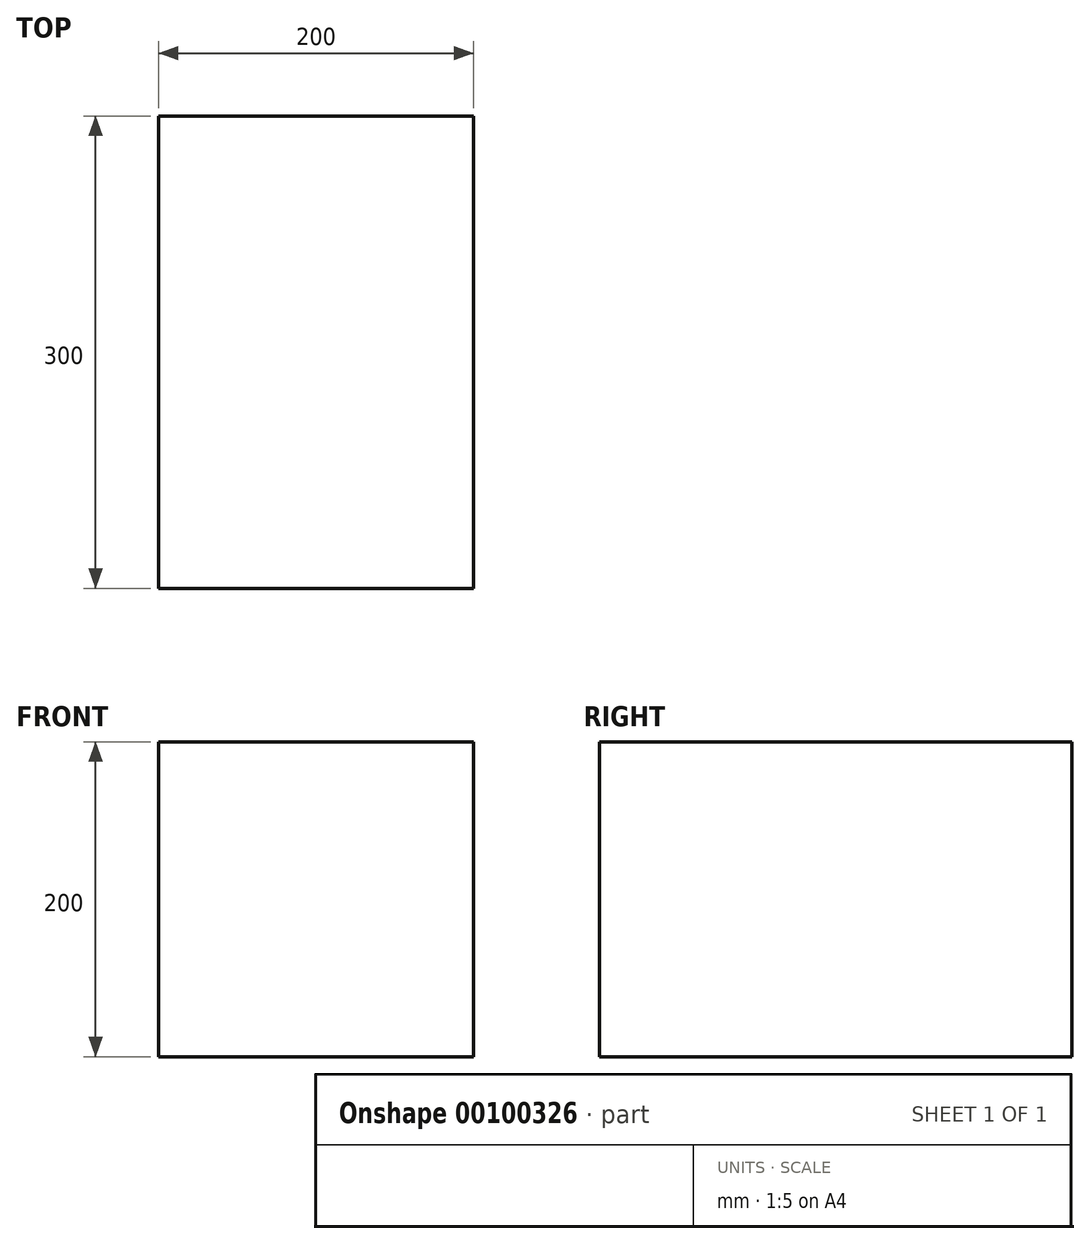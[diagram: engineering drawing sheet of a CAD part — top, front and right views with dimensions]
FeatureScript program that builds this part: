
annotation { "Feature Type Name" : "Feature", "Feature Type Description" : "" }
export const myFeature = defineFeature(function(context is Context, id is Id, definition is map)
    precondition{}
    {
        {
            var Q0;
            Q0=qCreatedBy(makeId("Front.planeOp"),FACE);
            var sketch = newSketch(context, id + "F0", { "sketchPlane" : qUnion([Q0])});
            skLineSegment(sketch, "E0.bottom", {"start": v(-98.75, 112.83) * mm, "end": v(101.25, 112.83) * mm});
            skLineSegment(sketch, "E0.top", {"start": v(-98.75, -87.17) * mm, "end": v(101.25, -87.17) * mm});
            skLineSegment(sketch, "E0.left", {"start": v(-98.75, 112.83) * mm, "end": v(-98.75, -87.17) * mm});
            skLineSegment(sketch, "E0.right", {"start": v(101.25, 112.83) * mm, "end": v(101.25, -87.17) * mm});
            skSolve(sketch);
        }
        {
            var Q0;
            Q0 = qSketchRegion(id + "F0", true);
            extrude(context, id + "F1", {"entities" : qUnion([Q0]), "depth" : 300 * mm});
        }
    });
